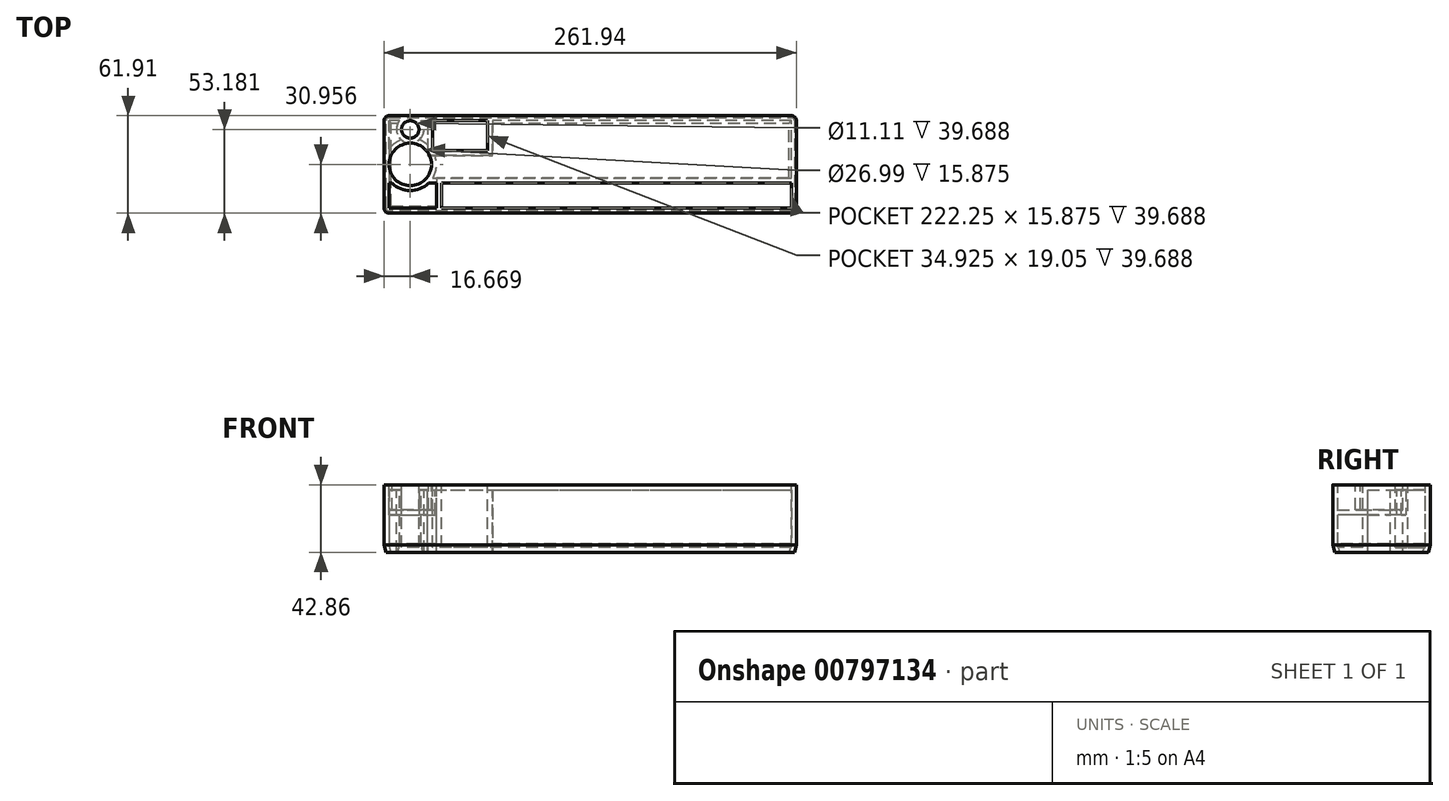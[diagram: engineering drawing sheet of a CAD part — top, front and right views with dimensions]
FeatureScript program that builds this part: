
annotation { "Feature Type Name" : "Feature", "Feature Type Description" : "" }
export const myFeature = defineFeature(function(context is Context, id is Id, definition is map)
    precondition{}
    {
        {
            var Q0;
            Q0=qCreatedBy(makeId("Top.planeOp"),FACE);
            var sketch = newSketch(context, id + "F0", { "sketchPlane" : qUnion([Q0])});
            skLineSegment(sketch, "E0.bottom", {"start": v(0, 0) * mm, "end": v(261.94, 0) * mm});
            skLineSegment(sketch, "E0.top", {"start": v(0, 61.91) * mm, "end": v(261.94, 61.91) * mm});
            skLineSegment(sketch, "E0.left", {"start": v(0, 0) * mm, "end": v(0, 61.91) * mm});
            skLineSegment(sketch, "E0.right", {"start": v(261.94, 0) * mm, "end": v(261.94, 61.91) * mm});
            skSolve(sketch);
        }
        {
            var Q0;
            Q0=qSketchRegion(id+"F0",true);
            extrude(context, id + "F1", {"entities" : qUnion([Q0]), "depth" : 42.86 * mm, "offsetDistance" : 25.4 * mm});
        }
        {
            var Q0;
            Q0=makeQuery(id+"F1.opExtrude","CAP_FACE",FACE,{"disambiguationData":[OSD([sQuery(id+"F0.wireOp",EDGE,"E0.bottom"),sQuery(id+"F0.wireOp",EDGE,"E0.top"),sQuery(id+"F0.wireOp",EDGE,"E0.left"),sQuery(id+"F0.wireOp",EDGE,"E0.right")])],"isStart":false});
            var sketch = newSketch(context, id + "F2", { "sketchPlane" : qUnion([Q0])});
            skLineSegment(sketch, "E1", {"start": v(0, 0) * mm, "end": v(0, 61.91) * mm, "construction": true});
            skLineSegment(sketch, "E2", {"start": v(0, 0) * mm, "end": v(261.94, 0) * mm, "construction": true});
            skCircle(sketch, "E3", {"center": v(16.67, 53.18) * mm, "radius": 5.56 * mm});
            skCircle(sketch, "E4", {"center": v(16.67, 30.96) * mm, "radius": 13.5 * mm, "construction": true});
            skLineSegment(sketch, "E5.bottom", {"start": v(30.87, 58.74) * mm, "end": v(65.8, 58.74) * mm});
            skLineSegment(sketch, "E5.top", {"start": v(30.87, 39.69) * mm, "end": v(65.8, 39.69) * mm});
            skLineSegment(sketch, "E5.left", {"start": v(30.87, 58.74) * mm, "end": v(30.87, 39.69) * mm});
            skLineSegment(sketch, "E5.right", {"start": v(65.8, 58.74) * mm, "end": v(65.8, 39.69) * mm});
            skLineSegment(sketch, "E6.bottom", {"start": v(36.51, 3.17) * mm, "end": v(258.76, 3.17) * mm});
            skLineSegment(sketch, "E6.top", {"start": v(36.51, 19.05) * mm, "end": v(258.76, 19.05) * mm});
            skLineSegment(sketch, "E6.left", {"start": v(36.51, 3.17) * mm, "end": v(36.51, 19.05) * mm});
            skLineSegment(sketch, "E6.right", {"start": v(258.76, 3.18) * mm, "end": v(258.76, 19.05) * mm});
            skLineSegment(sketch, "E7.bottom", {"start": v(3.17, 58.74) * mm, "end": v(258.76, 58.74) * mm, "construction": true});
            skLineSegment(sketch, "E7.top", {"start": v(3.17, 3.18) * mm, "end": v(258.76, 3.18) * mm, "construction": true});
            skLineSegment(sketch, "E7.left", {"start": v(3.17, 58.74) * mm, "end": v(3.17, 3.17) * mm, "construction": true});
            skLineSegment(sketch, "E7.right", {"start": v(258.76, 58.74) * mm, "end": v(258.76, 3.17) * mm, "construction": true});
            skLineSegment(sketch, "E8.bottom", {"start": v(3.17, 3.18) * mm, "end": v(33.34, 3.18) * mm, "construction": true});
            skLineSegment(sketch, "E8.top", {"start": v(3.17, 19.05) * mm, "end": v(5, 19.05) * mm, "construction": true});
            skLineSegment(sketch, "E8.left", {"start": v(3.17, 3.18) * mm, "end": v(3.17, 19.05) * mm, "construction": true});
            skLineSegment(sketch, "E8.right", {"start": v(33.34, 3.17) * mm, "end": v(33.34, 19.05) * mm, "construction": true});
            skArc(sketch, "E9", {"start": v(5, 19.05) * mm, "mid": v(16.67, 14.29) * mm, "end": v(28.33, 19.05) * mm, "construction": true});
            skLineSegment(sketch, "E10.trimOffspring", {"start": v(28.33, 19.05) * mm, "end": v(33.34, 19.05) * mm, "construction": true});
            skLineSegment(sketch, "E11", {"start": v(16.67, 53.18) * mm, "end": v(16.67, 30.96) * mm, "construction": true});
            skSolve(sketch);
        }
        {
            var Q0;
            Q0=qSketchRegion(id+"F2",true);
            var Q1;
            Q1=makeQuery(id+"F1.opExtrude","CAP_FACE",FACE,{"disambiguationData":[OSD([sQuery(id+"F0.wireOp",EDGE,"E0.bottom"),sQuery(id+"F0.wireOp",EDGE,"E0.top"),sQuery(id+"F0.wireOp",EDGE,"E0.left"),sQuery(id+"F0.wireOp",EDGE,"E0.right")])],"isStart":true});
            extrude(context, id + "F3", {"entities" : qUnion([Q0]), "operationType" : NewBodyOperationType.REMOVE, "endBound" : BoundingType.UP_TO_SURFACE, "oppositeDirection" : true, "depth" : 28.57 * mm, "endBoundEntityFace" : qUnion([Q1]), "hasOffset" : true, "offsetDistance" : 3.17 * mm});
        }
        {
            var Q0;
            Q0=makeQuery(id+"F2.imprint","IMPRINT",FACE,{"disambiguationData":[TD([[makeQuery(id+"F2.imprint","IMPRINT",EDGE,{"derivedFrom":sQuery(id+"F2.wireOp",EDGE,"E3")}),-1.0]])]});
            var sketch = newSketch(context, id + "F4", { "sketchPlane" : qUnion([Q0])});
            skLineSegment(sketch, "E12.0", {"start": v(0, 0) * mm, "end": v(0, 61.91) * mm});
            skLineSegment(sketch, "E12.1", {"start": v(0, 0) * mm, "end": v(261.94, 0) * mm, "construction": true});
            skCircle(sketch, "E12.2", {"center": v(16.67, 53.18) * mm, "radius": 5.56 * mm, "construction": true});
            skCircle(sketch, "E12.3", {"center": v(16.67, 30.96) * mm, "radius": 13.5 * mm});
            skLineSegment(sketch, "E12.4", {"start": v(30.87, 58.74) * mm, "end": v(65.8, 58.74) * mm, "construction": true});
            skLineSegment(sketch, "E12.5", {"start": v(30.87, 39.69) * mm, "end": v(65.8, 39.69) * mm, "construction": true});
            skLineSegment(sketch, "E12.6", {"start": v(30.87, 58.74) * mm, "end": v(30.87, 39.69) * mm, "construction": true});
            skLineSegment(sketch, "E12.7", {"start": v(65.8, 58.74) * mm, "end": v(65.8, 39.69) * mm, "construction": true});
            skLineSegment(sketch, "E12.8", {"start": v(36.51, 3.17) * mm, "end": v(258.76, 3.17) * mm, "construction": true});
            skLineSegment(sketch, "E12.9", {"start": v(36.51, 19.05) * mm, "end": v(258.76, 19.05) * mm, "construction": true});
            skLineSegment(sketch, "E12.10", {"start": v(36.51, 3.17) * mm, "end": v(36.51, 19.05) * mm, "construction": true});
            skLineSegment(sketch, "E12.11", {"start": v(258.76, 3.18) * mm, "end": v(258.76, 19.05) * mm, "construction": true});
            skLineSegment(sketch, "E12.12", {"start": v(3.17, 58.74) * mm, "end": v(258.76, 58.74) * mm, "construction": true});
            skLineSegment(sketch, "E12.13", {"start": v(3.17, 3.18) * mm, "end": v(258.76, 3.18) * mm, "construction": true});
            skLineSegment(sketch, "E12.14", {"start": v(3.17, 58.74) * mm, "end": v(3.17, 3.17) * mm, "construction": true});
            skLineSegment(sketch, "E12.15", {"start": v(258.76, 58.74) * mm, "end": v(258.76, 3.17) * mm, "construction": true});
            skLineSegment(sketch, "E12.16", {"start": v(3.17, 3.18) * mm, "end": v(33.34, 3.18) * mm});
            skLineSegment(sketch, "E12.17", {"start": v(3.17, 19.05) * mm, "end": v(5, 19.05) * mm});
            skLineSegment(sketch, "E12.18", {"start": v(3.17, 3.18) * mm, "end": v(3.17, 19.05) * mm});
            skLineSegment(sketch, "E12.19", {"start": v(33.34, 3.17) * mm, "end": v(33.34, 19.05) * mm});
            skArc(sketch, "E12.20", {"start": v(5, 19.05) * mm, "mid": v(16.67, 14.29) * mm, "end": v(28.33, 19.05) * mm});
            skLineSegment(sketch, "E12.21", {"start": v(28.33, 19.05) * mm, "end": v(33.34, 19.05) * mm});
            skLineSegment(sketch, "E12.22", {"start": v(16.67, 53.18) * mm, "end": v(16.67, 30.96) * mm, "construction": true});
            skSolve(sketch);
        }
        {
            var Q0;
            Q0=qSketchRegion(id+"F4",true);
            extrude(context, id + "F5", {"entities" : qUnion([Q0]), "operationType" : NewBodyOperationType.REMOVE, "oppositeDirection" : true, "depth" : 19.05 * mm - 3.17 * mm, "offsetDistance" : 25.4 * mm});
        }
        {
            var Q0;
            Q0=makeQuery(id+"F1.opExtrude","SWEPT_EDGE",EDGE,{"disambiguationData":[OSD([sQuery(id+"F0.wireOp",EDGE,"E0.bottom"),sQuery(id+"F0.wireOp",EDGE,"E0.left")])]});
            var Q1;
            Q1=makeQuery(id+"F1.opExtrude","SWEPT_EDGE",EDGE,{"disambiguationData":[OSD([sQuery(id+"F0.wireOp",EDGE,"E0.bottom"),sQuery(id+"F0.wireOp",EDGE,"E0.right")])]});
            var Q2;
            Q2=makeQuery(id+"F1.opExtrude","SWEPT_EDGE",EDGE,{"disambiguationData":[OSD([sQuery(id+"F0.wireOp",EDGE,"E0.top"),sQuery(id+"F0.wireOp",EDGE,"E0.right")])]});
            var Q3;
            Q3=makeQuery(id+"F1.opExtrude","SWEPT_EDGE",EDGE,{"disambiguationData":[OSD([sQuery(id+"F0.wireOp",EDGE,"E0.top"),sQuery(id+"F0.wireOp",EDGE,"E0.left")])]});
            fillet(context, id + "F6", {"entities" : qUnion([Q0, Q1, Q2, Q3]), "radius" : 3.17 * mm, "tangentPropagation" : true, "allowEdgeOverflow" : false});
        }
        {
            var Q0;
            Q0=makeQuery(id+"F1.opExtrude","CAP_EDGE",EDGE,{"disambiguationData":[OSD([sQuery(id+"F0.wireOp",EDGE,"E0.top")])],"isStart":true});
            chamfer(context, id + "F7", {"entities" : qUnion([Q0]), "chamferType" : ChamferType.OFFSET_ANGLE, "width" : 4.76 * mm, "oppositeDirection" : true, "angle" : 15 * degree, "tangentPropagation" : true});
        }
        {
            var Q0;
            Q0=makeQuery(id+"F1.opExtrude","CAP_FACE",FACE,{"disambiguationData":[OSD([sQuery(id+"F0.wireOp",EDGE,"E0.bottom"),sQuery(id+"F0.wireOp",EDGE,"E0.top"),sQuery(id+"F0.wireOp",EDGE,"E0.left"),sQuery(id+"F0.wireOp",EDGE,"E0.right")])],"isStart":true});
            shell(context, id + "F8", {"entities" : qUnion([Q0]), "thickness" : 3.17 * mm});
        }
    });
